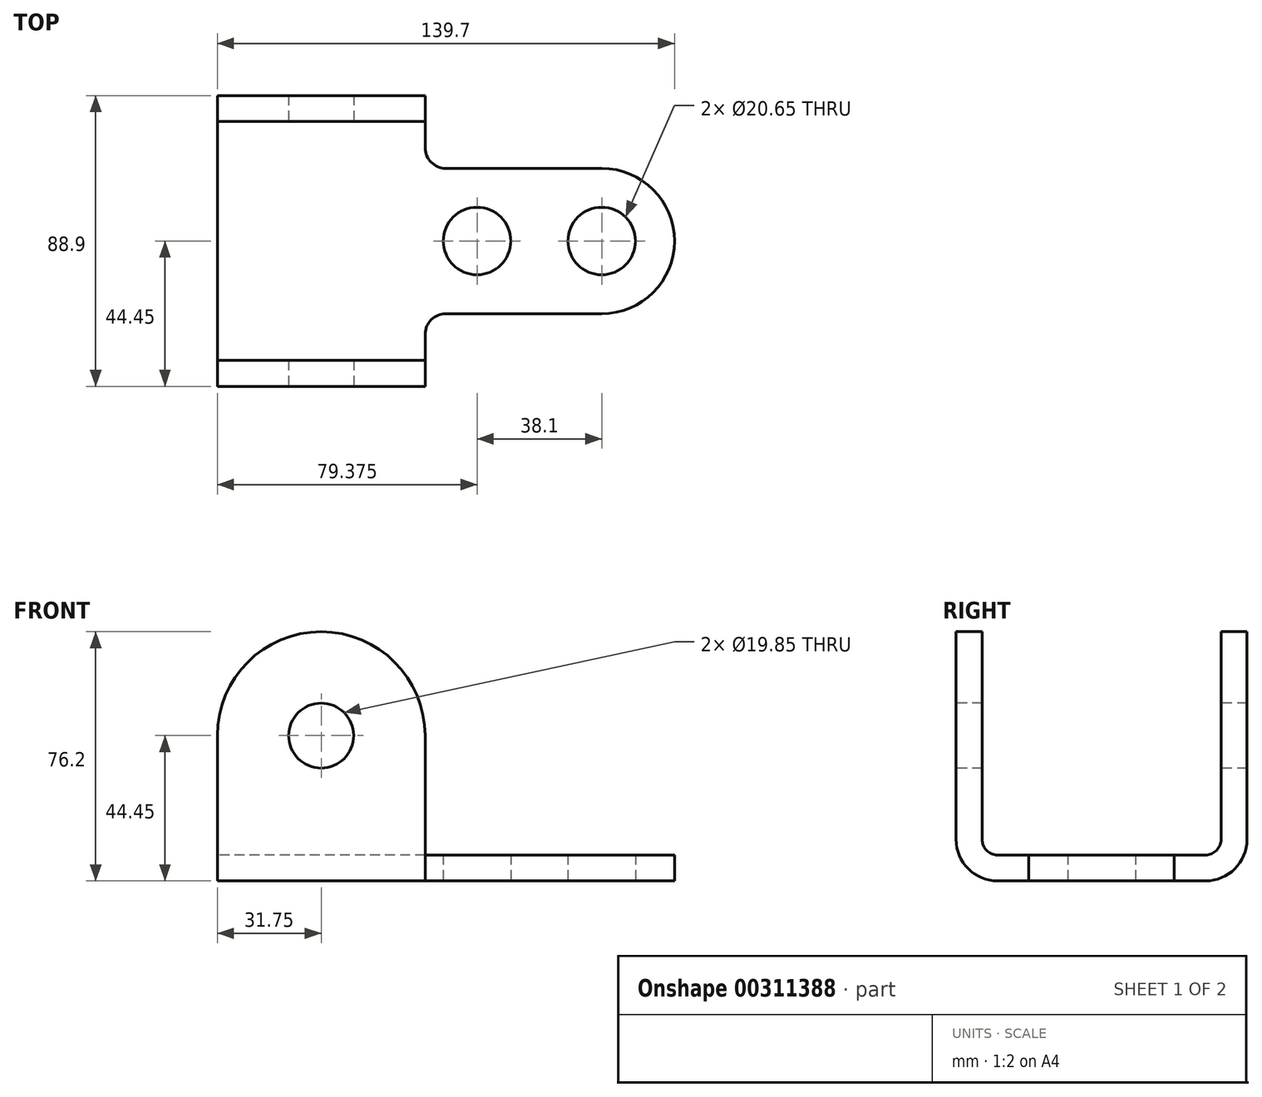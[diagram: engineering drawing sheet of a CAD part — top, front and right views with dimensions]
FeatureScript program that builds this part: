
annotation { "Feature Type Name" : "Feature", "Feature Type Description" : "" }
export const myFeature = defineFeature(function(context is Context, id is Id, definition is map)
    precondition{}
    {
        {
            var Q0;
            Q0=qCreatedBy(makeId("Top.planeOp"),FACE);
            var sketch = newSketch(context, id + "F0", { "sketchPlane" : qUnion([Q0])});
            skLineSegment(sketch, "E0", {"start": v(0, 0) * mm, "end": v(139.7, 0) * mm, "construction": true});
            skLineSegment(sketch, "E1", {"start": v(0, 44.45) * mm, "end": v(0, -44.45) * mm});
            skLineSegment(sketch, "E2", {"start": v(0, 44.45) * mm, "end": v(63.5, 44.45) * mm});
            skLineSegment(sketch, "E3", {"start": v(0, -44.45) * mm, "end": v(63.5, -44.45) * mm});
            skPoint(sketch, "E4", {"position": v(63.5, 0) * mm});
            skPoint(sketch, "E5", {"position": v(79.38, 0) * mm});
            skPoint(sketch, "E6", {"position": v(117.48, 0) * mm});
            skCircle(sketch, "E7", {"center": v(79.38, 0) * mm, "radius": 10.33 * mm});
            skCircle(sketch, "E8", {"center": v(117.48, 0) * mm, "radius": 10.33 * mm});
            skLineSegment(sketch, "E9", {"start": v(63.5, 44.45) * mm, "end": v(63.5, 28.58) * mm});
            skArc(sketch, "E10", {"start": v(63.5, 28.58) * mm, "mid": v(65.36, 24.08) * mm, "end": v(69.85, 22.23) * mm});
            skLineSegment(sketch, "E11", {"start": v(63.5, -44.45) * mm, "end": v(63.5, -28.58) * mm});
            skArc(sketch, "E12", {"start": v(69.85, -22.23) * mm, "mid": v(65.36, -24.08) * mm, "end": v(63.5, -28.58) * mm});
            skLineSegment(sketch, "E13", {"start": v(69.85, 22.23) * mm, "end": v(117.48, 22.23) * mm});
            skLineSegment(sketch, "E14", {"start": v(69.85, -22.23) * mm, "end": v(117.48, -22.23) * mm});
            skArc(sketch, "E15", {"start": v(117.48, -22.23) * mm, "mid": v(139.7, 0) * mm, "end": v(117.48, 22.23) * mm});
            skSolve(sketch);
        }
        {
            var Q0;
            Q0=makeQuery(id+"F0.imprint","IMPRINT",FACE,{"disambiguationData":[TD([[makeQuery(id+"F0.imprint","IMPRINT",EDGE,{"derivedFrom":sQuery(id+"F0.wireOp",EDGE,"E1")}),1.0]])]});
            extrude(context, id + "F1", {"entities" : qUnion([Q0]), "depth" : 7.94 * mm});
        }
        {
            var Q0;
            Q0=makeQuery(id+"F1.opExtrude","CAP_FACE",FACE,{"disambiguationData":[OSD([sQuery(id+"F0.wireOp",EDGE,"E1"),sQuery(id+"F0.wireOp",EDGE,"E2"),sQuery(id+"F0.wireOp",EDGE,"E3"),sQuery(id+"F0.wireOp",EDGE,"E7"),sQuery(id+"F0.wireOp",EDGE,"E8"),sQuery(id+"F0.wireOp",EDGE,"E9"),sQuery(id+"F0.wireOp",EDGE,"E10"),sQuery(id+"F0.wireOp",EDGE,"E11"),sQuery(id+"F0.wireOp",EDGE,"E12"),sQuery(id+"F0.wireOp",EDGE,"E13"),sQuery(id+"F0.wireOp",EDGE,"E14"),sQuery(id+"F0.wireOp",EDGE,"E15")])],"isStart":false});
            var sketch = newSketch(context, id + "F2", { "sketchPlane" : qUnion([Q0])});
            skLineSegment(sketch, "E16", {"start": v(0, -44.45) * mm, "end": v(0, -36.51) * mm});
            skLineSegment(sketch, "E17", {"start": v(0, 44.45) * mm, "end": v(0, 36.51) * mm});
            skLineSegment(sketch, "E18", {"start": v(0, 36.51) * mm, "end": v(63.5, 36.51) * mm});
            skLineSegment(sketch, "E19", {"start": v(63.5, 36.51) * mm, "end": v(63.5, 44.45) * mm});
            skLineSegment(sketch, "E20", {"start": v(63.5, 44.45) * mm, "end": v(0, 44.45) * mm});
            skLineSegment(sketch, "E21", {"start": v(0, -36.51) * mm, "end": v(63.5, -36.51) * mm});
            skLineSegment(sketch, "E22", {"start": v(63.5, -36.51) * mm, "end": v(63.5, -44.45) * mm});
            skLineSegment(sketch, "E23", {"start": v(63.5, -44.45) * mm, "end": v(0, -44.45) * mm});
            skSolve(sketch);
        }
        {
            var Q0;
            Q0 = qSketchRegion(id + "F2", true);
            extrude(context, id + "F3", {"entities" : qUnion([Q0]), "operationType" : NewBodyOperationType.ADD, "depth" : 68.26 * mm});
        }
        {
            var Q0;
            Q0=makeQuery(id+"F3.boolean.opBoolean","MERGE",FACE,{"derivedFrom":[makeQuery(id+"F1.opExtrude","SWEPT_FACE",FACE,{"disambiguationData":[OSD([sQuery(id+"F0.wireOp",EDGE,"E3")])]}),makeQuery(id+"F3.opExtrude","SWEPT_FACE",FACE,{"disambiguationData":[OSD([sQuery(id+"F2.wireOp",EDGE,"E23")])]})]});
            var sketch = newSketch(context, id + "F4", { "sketchPlane" : qUnion([Q0])});
            skLineSegment(sketch, "E24", {"start": v(31.75, 0) * mm, "end": v(31.75, 44.45) * mm, "construction": true});
            skCircle(sketch, "E25", {"center": v(31.75, 44.45) * mm, "radius": 9.92 * mm});
            skArc(sketch, "E26", {"start": v(63.5, 44.45) * mm, "mid": v(31.75, 76.2) * mm, "end": v(0, 44.45) * mm});
            skLineSegment(sketch, "E27", {"start": v(0, 44.45) * mm, "end": v(0, 0) * mm});
            skLineSegment(sketch, "E28", {"start": v(0, 0) * mm, "end": v(63.5, 0) * mm});
            skLineSegment(sketch, "E29", {"start": v(63.5, 0) * mm, "end": v(63.5, 44.45) * mm});
            skLineSegment(sketch, "E30", {"start": v(0, 44.45) * mm, "end": v(0, 76.2) * mm});
            skLineSegment(sketch, "E31", {"start": v(0, 76.2) * mm, "end": v(63.5, 76.2) * mm});
            skLineSegment(sketch, "E32", {"start": v(63.5, 76.2) * mm, "end": v(63.5, 44.45) * mm});
            skSolve(sketch);
        }
        {
            var Q0;
            {var subQ0=sQuery(id+"F4.wireOp",EDGE,"E30");Q0=makeQuery(id+"F4.imprint","IMPRINT",FACE,{"disambiguationData":[TD([[makeQuery(id+"F4.imprint","IMPRINT",EDGE,{"derivedFrom":subQ0}),1.0]])]});}
            var Q1;
            {var subQ0=sQuery(id+"F4.wireOp",EDGE,"E32");Q1=makeQuery(id+"F4.imprint","IMPRINT",FACE,{"disambiguationData":[TD([[makeQuery(id+"F4.imprint","IMPRINT",EDGE,{"derivedFrom":subQ0}),-1.0]])]});}
            var Q2;
            Q2=makeQuery(id+"F4.imprint","IMPRINT",FACE,{"disambiguationData":[TD([[makeQuery(id+"F4.imprint","IMPRINT",EDGE,{"derivedFrom":sQuery(id+"F4.wireOp",EDGE,"E25")}),1.0]])]});
            extrude(context, id + "F5", {"entities" : qUnion([Q0, Q1, Q2]), "operationType" : NewBodyOperationType.REMOVE, "endBound" : BoundingType.THROUGH_ALL, "oppositeDirection" : true, "depth" : 25.4 * mm});
        }
        {
            var Q0;
            Q0=qCreatedBy(makeId("Right.planeOp"),FACE);
            var sketch = newSketch(context, id + "F6", { "sketchPlane" : qUnion([Q0])});
            skArc(sketch, "E33", {"start": v(-36.51, 12.7) * mm, "mid": v(-35.12, 9.33) * mm, "end": v(-31.75, 7.94) * mm});
            skArc(sketch, "E34", {"start": v(-44.45, 12.7) * mm, "mid": v(-40.73, 3.72) * mm, "end": v(-31.75, 0) * mm});
            skArc(sketch, "E35", {"start": v(31.75, 0) * mm, "mid": v(40.73, 3.72) * mm, "end": v(44.45, 12.7) * mm});
            skArc(sketch, "E36", {"start": v(31.75, 7.94) * mm, "mid": v(35.12, 9.33) * mm, "end": v(36.51, 12.7) * mm});
            skLineSegment(sketch, "E37", {"start": v(-44.45, 12.7) * mm, "end": v(-44.45, 0) * mm});
            skLineSegment(sketch, "E38", {"start": v(-44.45, 0) * mm, "end": v(-31.75, 0) * mm});
            skLineSegment(sketch, "E39", {"start": v(44.45, 12.7) * mm, "end": v(44.45, 0) * mm});
            skLineSegment(sketch, "E40", {"start": v(44.45, 0) * mm, "end": v(31.75, 0) * mm});
            skLineSegment(sketch, "E41", {"start": v(36.51, 12.7) * mm, "end": v(36.51, 7.94) * mm});
            skLineSegment(sketch, "E42", {"start": v(36.51, 7.94) * mm, "end": v(31.75, 7.94) * mm});
            skLineSegment(sketch, "E43", {"start": v(-36.51, 12.7) * mm, "end": v(-36.51, 7.94) * mm});
            skLineSegment(sketch, "E44", {"start": v(-31.75, 7.94) * mm, "end": v(-36.51, 7.94) * mm});
            skSolve(sketch);
        }
        {
            var Q0;
            Q0=makeQuery(id+"F6.imprint","IMPRINT",FACE,{"disambiguationData":[TD([[makeQuery(id+"F6.imprint","IMPRINT",EDGE,{"derivedFrom":sQuery(id+"F6.wireOp",EDGE,"E34")}),-1.0]])]});
            var Q1;
            Q1=makeQuery(id+"F6.imprint","IMPRINT",FACE,{"disambiguationData":[TD([[makeQuery(id+"F6.imprint","IMPRINT",EDGE,{"derivedFrom":sQuery(id+"F6.wireOp",EDGE,"E35")}),-1.0]])]});
            extrude(context, id + "F7", {"entities" : qUnion([Q0, Q1]), "operationType" : NewBodyOperationType.REMOVE, "endBound" : BoundingType.THROUGH_ALL, "depth" : 25.4 * mm});
        }
        {
            var Q0;
            Q0=makeQuery(id+"F6.imprint","IMPRINT",FACE,{"disambiguationData":[TD([[makeQuery(id+"F6.imprint","IMPRINT",EDGE,{"derivedFrom":sQuery(id+"F6.wireOp",EDGE,"E36")}),-1.0]])]});
            var Q1;
            Q1=makeQuery(id+"F6.imprint","IMPRINT",FACE,{"disambiguationData":[TD([[makeQuery(id+"F6.imprint","IMPRINT",EDGE,{"derivedFrom":sQuery(id+"F6.wireOp",EDGE,"E33")}),-1.0]])]});
            extrude(context, id + "F8", {"entities" : qUnion([Q0, Q1]), "operationType" : NewBodyOperationType.ADD, "depth" : 63.5 * mm});
        }
    });
